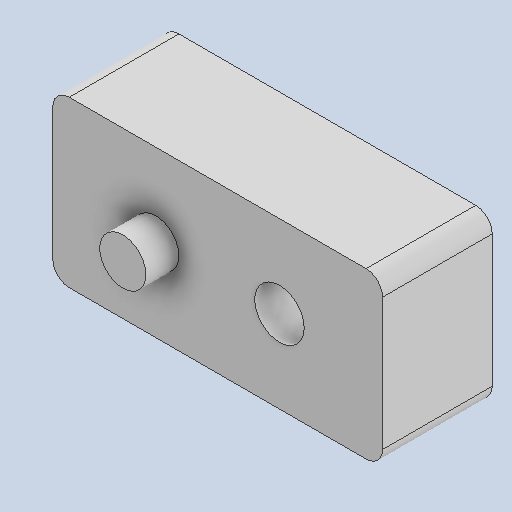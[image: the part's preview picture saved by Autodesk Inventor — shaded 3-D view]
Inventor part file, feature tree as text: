
AUTODESK INVENTOR PART (.ipt)
format: ipt  version: 2024.2 (Build 282272000, 272)  size: 123,904 bytes
history: native  units: mm
features: extrude x2, fillet x1
ambient origin geometry x8: Origin, YZ Plane, XZ Plane, XY Plane, X Axis, Y Axis, Z Axis, Center Point
bodies: Solid1 (feature_tree)
feature tree (3):
  extrude  "Extrusion1"  Depth=20.0mm
  extrude  "Extrusion2"  Depth=10.0mm
  fillet  "Fillet2"  Radius=3.0mm
